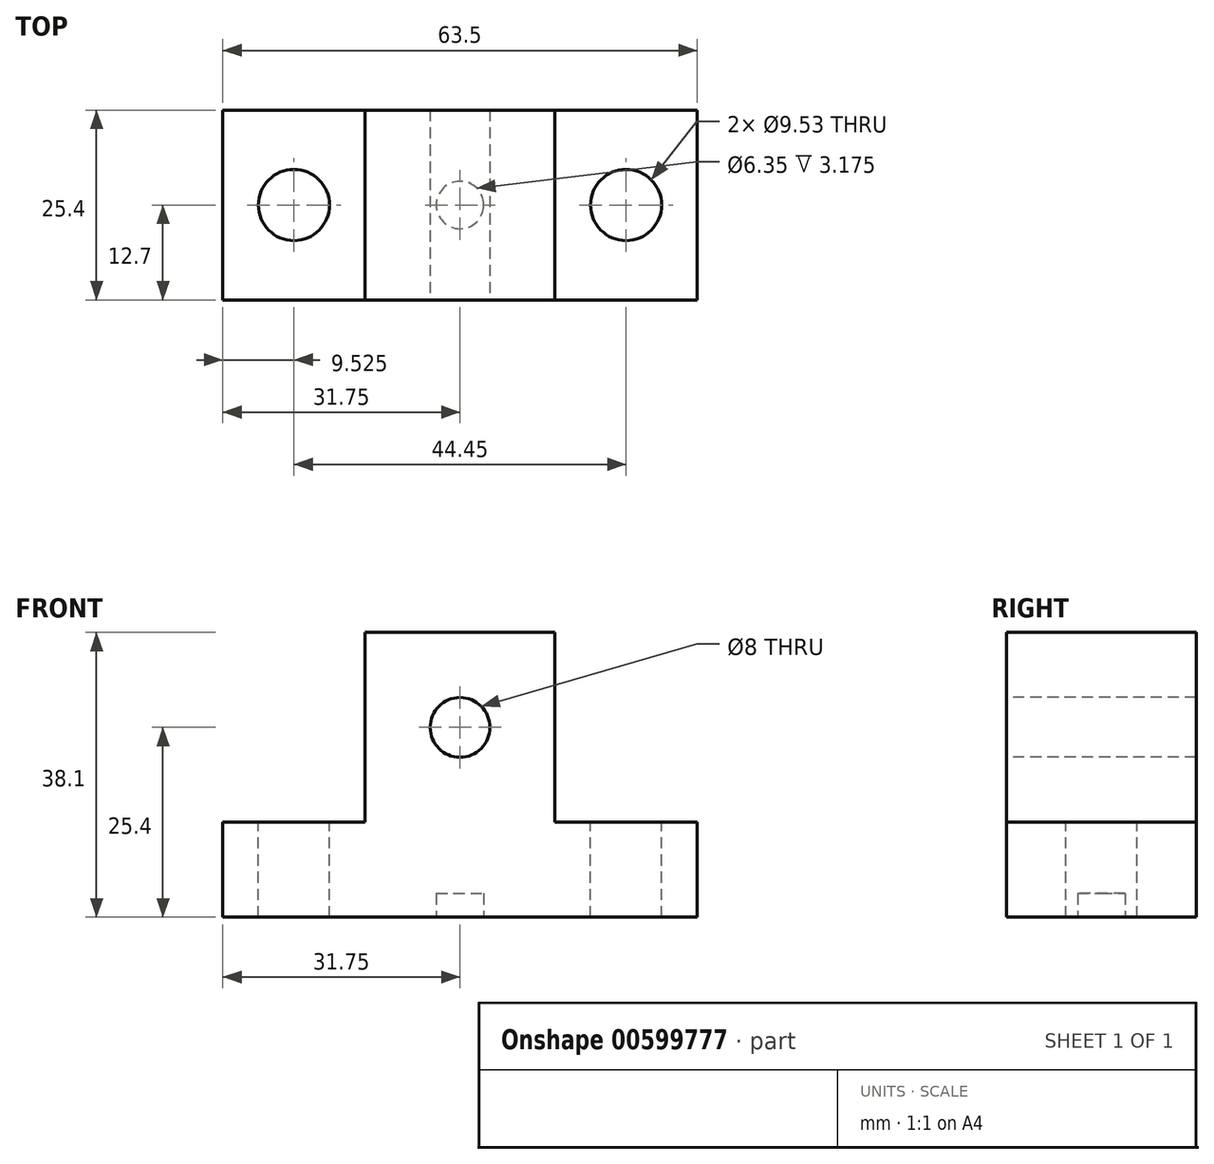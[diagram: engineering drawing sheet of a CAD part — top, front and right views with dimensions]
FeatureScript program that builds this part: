
annotation { "Feature Type Name" : "Feature", "Feature Type Description" : "" }
export const myFeature = defineFeature(function(context is Context, id is Id, definition is map)
    precondition{}
    {
        {
            var Q0;
            Q0=qCreatedBy(makeId("Front.planeOp"),FACE);
            var sketch = newSketch(context, id + "F0", { "sketchPlane" : qUnion([Q0])});
            skLineSegment(sketch, "E0", {"start": v(-31.75, 0) * mm, "end": v(31.75, 0) * mm});
            skLineSegment(sketch, "E1", {"start": v(31.75, 0) * mm, "end": v(31.75, 12.7) * mm});
            skLineSegment(sketch, "E2", {"start": v(31.75, 12.7) * mm, "end": v(12.7, 12.7) * mm});
            skLineSegment(sketch, "E3", {"start": v(12.7, 12.7) * mm, "end": v(12.7, 38.1) * mm});
            skLineSegment(sketch, "E4", {"start": v(12.7, 38.1) * mm, "end": v(-12.7, 38.1) * mm});
            skLineSegment(sketch, "E5", {"start": v(-12.7, 38.1) * mm, "end": v(-12.7, 12.7) * mm});
            skLineSegment(sketch, "E6", {"start": v(-12.7, 12.7) * mm, "end": v(-31.75, 12.7) * mm});
            skLineSegment(sketch, "E7", {"start": v(-31.75, 12.7) * mm, "end": v(-31.75, 0) * mm});
            skSolve(sketch);
        }
        {
            var Q0;
            Q0=makeQuery(id+"F0.imprint","IMPRINT",FACE,{"disambiguationData":[TD([[makeQuery(id+"F0.imprint","IMPRINT",EDGE,{"derivedFrom":sQuery(id+"F0.wireOp",EDGE,"E0")}),1.0]])]});
            extrude(context, id + "F1", {"entities" : qUnion([Q0]), "depth" : 25.4 * mm, "offsetDistance" : 25.4 * mm});
        }
        {
            var Q0;
            Q0=makeQuery(id+"F1.opExtrude","SWEPT_FACE",FACE,{"disambiguationData":[OSD([sQuery(id+"F0.wireOp",EDGE,"E6")])]});
            var sketch = newSketch(context, id + "F2", { "sketchPlane" : qUnion([Q0])});
            skCircle(sketch, "E8", {"center": v(-22.23, -12.7) * mm, "radius": 4.76 * mm});
            skPoint(sketch, "E8.centerSnap0", {"position": v(-31.75, -12.7) * mm});
            skPoint(sketch, "E8.centerSnap1", {"position": v(-22.23, 0) * mm});
            skSolve(sketch);
        }
        {
            var Q0;
            Q0 = qSketchRegion(id + "F2", true);
            extrude(context, id + "F3", {"entities" : qUnion([Q0]), "operationType" : NewBodyOperationType.REMOVE, "endBound" : BoundingType.THROUGH_ALL, "oppositeDirection" : true, "depth" : 25.4 * mm, "offsetDistance" : 25.4 * mm});
        }
        {
            var Q0;
            Q0=makeQuery(id+"F1.opExtrude","SWEPT_FACE",FACE,{"disambiguationData":[OSD([sQuery(id+"F0.wireOp",EDGE,"E2")])]});
            var sketch = newSketch(context, id + "F4", { "sketchPlane" : qUnion([Q0])});
            skCircle(sketch, "E9", {"center": v(22.22, -12.7) * mm, "radius": 4.76 * mm});
            skPoint(sketch, "E9.centerSnap0", {"position": v(22.23, -25.4) * mm});
            skPoint(sketch, "E9.centerSnap1", {"position": v(31.75, -12.7) * mm});
            skSolve(sketch);
        }
        {
            var Q0;
            Q0 = qSketchRegion(id + "F4", true);
            extrude(context, id + "F5", {"entities" : qUnion([Q0]), "operationType" : NewBodyOperationType.REMOVE, "endBound" : BoundingType.THROUGH_ALL, "oppositeDirection" : true, "depth" : 25.4 * mm, "offsetDistance" : 25.4 * mm});
        }
        {
            var Q0;
            Q0=makeQuery(id+"F1.opExtrude","CAP_FACE",FACE,{"disambiguationData":[OSD([sQuery(id+"F0.wireOp",EDGE,"E0"),sQuery(id+"F0.wireOp",EDGE,"E1"),sQuery(id+"F0.wireOp",EDGE,"E2"),sQuery(id+"F0.wireOp",EDGE,"E3"),sQuery(id+"F0.wireOp",EDGE,"E4"),sQuery(id+"F0.wireOp",EDGE,"E5"),sQuery(id+"F0.wireOp",EDGE,"E6"),sQuery(id+"F0.wireOp",EDGE,"E7")])],"isStart":false});
            var sketch = newSketch(context, id + "F6", { "sketchPlane" : qUnion([Q0])});
            skCircle(sketch, "E10", {"center": v(0, 25.4) * mm, "radius": 4 * mm});
            skPoint(sketch, "E10.centerSnap0", {"position": v(12.7, 25.4) * mm});
            skPoint(sketch, "E10.centerSnap1", {"position": v(0, 38.1) * mm});
            skSolve(sketch);
        }
        {
            var Q0;
            Q0 = qSketchRegion(id + "F6", true);
            extrude(context, id + "F7", {"entities" : qUnion([Q0]), "operationType" : NewBodyOperationType.REMOVE, "endBound" : BoundingType.THROUGH_ALL, "oppositeDirection" : true, "depth" : 25.4 * mm, "offsetDistance" : 25.4 * mm});
        }
        {
            var Q0;
            Q0=makeQuery(id+"F1.opExtrude","SWEPT_FACE",FACE,{"disambiguationData":[OSD([sQuery(id+"F0.wireOp",EDGE,"E0")])]});
            var sketch = newSketch(context, id + "F8", { "sketchPlane" : qUnion([Q0])});
            skLineSegment(sketch, "E11", {"start": v(0, 25.4) * mm, "end": v(0, 0) * mm, "construction": true});
            skCircle(sketch, "E12", {"center": v(0, 12.7) * mm, "radius": 3.18 * mm});
            skSolve(sketch);
        }
        {
            var Q0;
            Q0 = qSketchRegion(id + "F8", true);
            extrude(context, id + "F9", {"entities" : qUnion([Q0]), "operationType" : NewBodyOperationType.REMOVE, "oppositeDirection" : true, "depth" : 3.17 * mm, "offsetDistance" : 25.4 * mm});
        }
    });
